# Revit family: Deca_Ducha Higiênica Link_1984.C.ACT.LNK.CR
name_source: partatom
category: Plumbing Fixtures
revit_build: Autodesk Revit Architecture 2012 (Build: 20110916_2132(x64)
units: mm (PartAtom-declared; Revit-internal decimal feet)

## types (2) — shared parameters
Aprovado por = Contino/quattroD
Assembly Code = D2010710
Atendimento ao Cliente = 0800-0117073
Consumo = Varia com a pressão
Criado por = Contino/quattroD
Default Elevation = 1200 mm
Description = Ducha higiênica com registro
Diâmetro Água Fria = 15 mm  [stored 0.0492126 ft]
Ducha Higiênica = Deca CR10 Cromado Metal
Flow Pressure = 0.00 psi
Informações Complementares = Mecanismo: 3 1/2 de volta
Linha = Link
Louça/Metais = Metal
Manufacturer = Deca
Material = Deca_Latão Cromado e Plástico de Engenharia
Norma = ABNT NBR 14877: 2002
Peso Liquido (Kg) = 0.71
Pressão = 2 A 40 mca
Produto = Ducha higiênica
Raio Água Fria = 8 mm  [stored 0.0262467 ft]
Segmento = Competitivo
URL = www.deca.com.br/produtos
Variações de COR = Gatilho cromado (1984.C.ACT.LNK.CR), gatilho branco (1984.C.ACT.LNK.BR)
zero-valued in all types: CWFU

## per-type parameters (varying)
| type | Código | Gatilho | Model |
| 1984.C.ACT.LNK.CR_Cromado CR10 | 1984.C.ACT.LNK.CR | Deca CR10 Cromado Metal | 1984.C.ACT.LNK.CR |
| 1984.C.ACT.LNK.BR_Branco BR16 | 1984.C.ACT.LNK.BR | Deca BR16 Branco Metal | 1984.C.ACT.LNK.BR |

note: [stored X ft] marks values corroborated as IEEE doubles in the binary element streams (Revit-internal decimal feet)

## geometry (parser evidence)
native form markers: Blend x2, Sweep x3
no freeform markers — native parametric forms only
